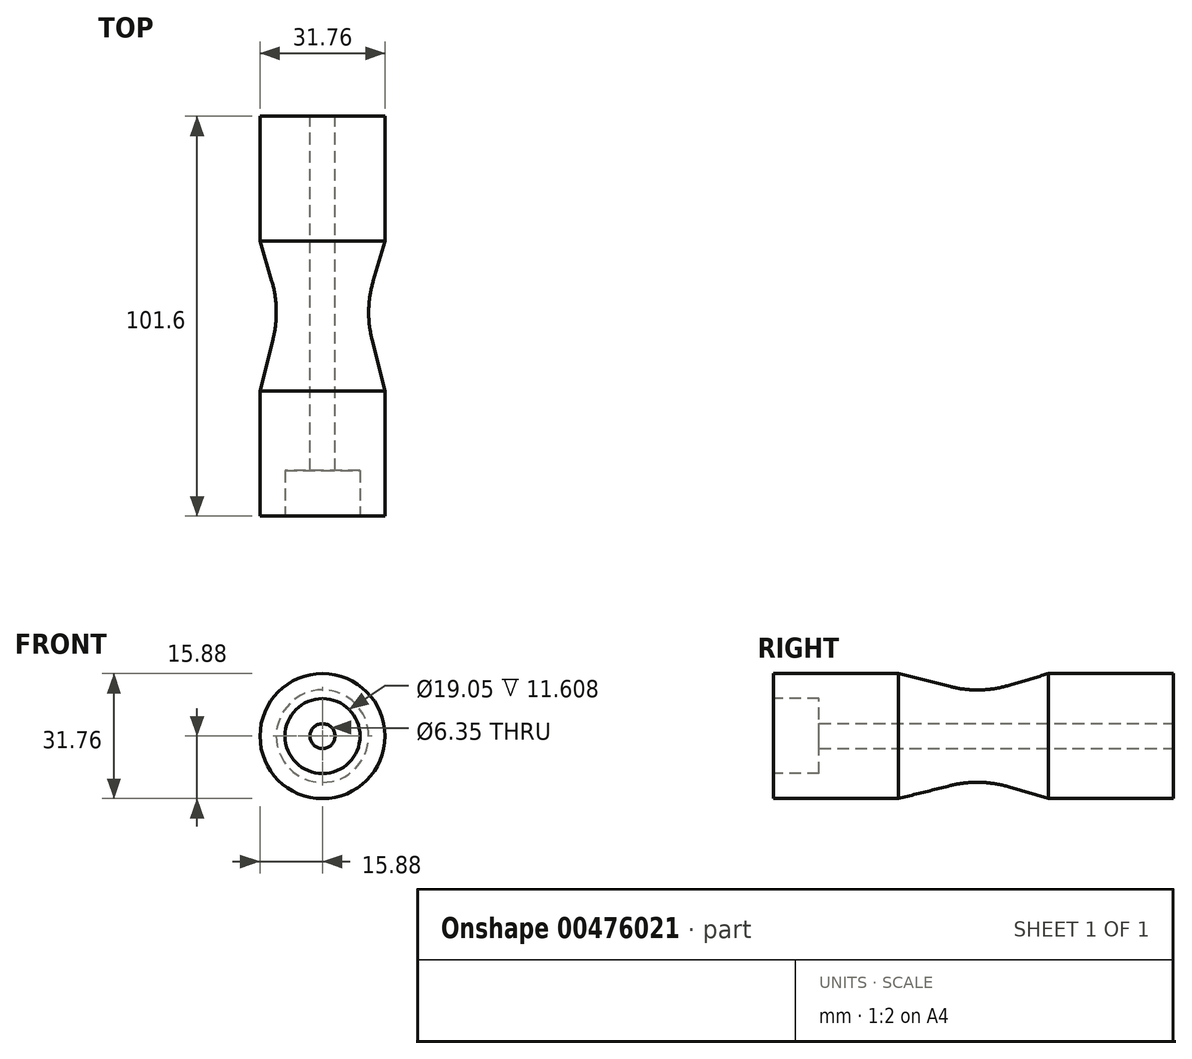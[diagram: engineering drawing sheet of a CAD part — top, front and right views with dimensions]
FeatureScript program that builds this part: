
annotation { "Feature Type Name" : "Feature", "Feature Type Description" : "" }
export const myFeature = defineFeature(function(context is Context, id is Id, definition is map)
    precondition{}
    {
        {
            var Q0;
            Q0=qCreatedBy(makeId("Right.planeOp"),FACE);
            var sketch = newSketch(context, id + "F0", { "sketchPlane" : qUnion([Q0])});
            skLineSegment(sketch, "E0", {"start": v(0, 0) * mm, "end": v(0, 15.88) * mm});
            skLineSegment(sketch, "E1", {"start": v(0, 15.88) * mm, "end": v(31.75, 15.88) * mm});
            skLineSegment(sketch, "E2", {"start": v(69.85, 15.88) * mm, "end": v(101.6, 15.88) * mm});
            skLineSegment(sketch, "E3", {"start": v(101.6, 15.88) * mm, "end": v(101.6, 0) * mm});
            skLineSegment(sketch, "E4", {"start": v(-52.77, 0) * mm, "end": v(123.31, 0) * mm, "construction": true});
            skLineSegment(sketch, "E5", {"start": v(0, 0) * mm, "end": v(101.6, 0) * mm});
            skLineSegment(sketch, "E6", {"start": v(48.26, 11.73) * mm, "end": v(55.88, 11.73) * mm});
            skLineSegment(sketch, "E7", {"start": v(48.26, 11.73) * mm, "end": v(31.75, 15.88) * mm});
            skLineSegment(sketch, "E8", {"start": v(55.88, 11.73) * mm, "end": v(69.85, 15.88) * mm});
            skSolve(sketch);
        }
        {
            var Q0;
            Q0 = qSketchRegion(id + "F0", true);
            var Q1;
            Q1=sQuery(id+"F0.wireOp",EDGE,"E4");
            revolve(context, id + "F1", {"entities" : qUnion([Q0]), "axis" : qUnion([Q1]), "revolveType" : RevolveType.FULL});
        }
        {
            var Q0;
            Q0=makeQuery(id+"F1.opRevolve","SWEPT_FACE",FACE,{"disambiguationData":[OSD([sQuery(id+"F0.wireOp",EDGE,"E0")])]});
            var sketch = newSketch(context, id + "F2", { "sketchPlane" : qUnion([Q0])});
            skCircle(sketch, "E9", {"center": v(0, 0) * mm, "radius": 9.53 * mm});
            skSolve(sketch);
        }
        {
            var Q0;
            Q0=makeQuery(id+"F2.imprint","IMPRINT",FACE,{"disambiguationData":[TD([[makeQuery(id+"F2.imprint","IMPRINT",EDGE,{"derivedFrom":sQuery(id+"F2.wireOp",EDGE,"E9")}),1.0]])]});
            extrude(context, id + "F3", {"entities" : qUnion([Q0]), "operationType" : NewBodyOperationType.REMOVE, "oppositeDirection" : true, "depth" : 11.6 * mm});
        }
        {
            var Q0;
            Q0=makeQuery(id+"F1.opRevolve","SWEPT_FACE",FACE,{"disambiguationData":[OSD([sQuery(id+"F0.wireOp",EDGE,"E3")])]});
            var sketch = newSketch(context, id + "F4", { "sketchPlane" : qUnion([Q0])});
            skPoint(sketch, "E10", {"position": v(0, 0) * mm});
            skSolve(sketch);
        }
        {
            var Q0;
            Q0=sQuery(id+"F4.wireOp",VERTEX,"E10");
            var Q1;
            Q1=makeQuery(id+"F1.opRevolve","SWEPT_BODY",BODY,{"disambiguationData":[OSD([sQuery(id+"F0.wireOp",EDGE,"E0"),sQuery(id+"F0.wireOp",EDGE,"E1"),sQuery(id+"F0.wireOp",EDGE,"71327644-5866-43d5-a122-7f9d2be9e36c"),sQuery(id+"F0.wireOp",EDGE,"E2"),sQuery(id+"F0.wireOp",EDGE,"E3"),sQuery(id+"F0.wireOp",EDGE,"E5")])]});
            hole(context, id + "F5", {"style" : HoleStyle.SIMPLE, "endStyle" : HoleEndStyle.THROUGH, "holeDiameter" : 6.35 * mm, "isTappedThrough" : true, "tappedDepth" : 12.7 * mm, "tapClearance" : 3, "startFromSketch" : true, "locations" : qUnion([Q0]), "scope" : qUnion([Q1])});
        }
        {
            var Q0;
            Q0=makeQuery(id+"F1.opRevolve","SWEPT_EDGE",EDGE,{"disambiguationData":[OSD([sQuery(id+"F0.wireOp",EDGE,"E6"),sQuery(id+"F0.wireOp",EDGE,"E7")])]});
            var Q1;
            Q1=makeQuery(id+"F1.opRevolve","SWEPT_EDGE",EDGE,{"disambiguationData":[OSD([sQuery(id+"F0.wireOp",EDGE,"E6"),sQuery(id+"F0.wireOp",EDGE,"E8")])]});
            fillet(context, id + "F6", {"entities" : qUnion([Q0, Q1]), "radius" : 27.94 * mm, "tangentPropagation" : true, "allowEdgeOverflow" : false});
        }
    });
